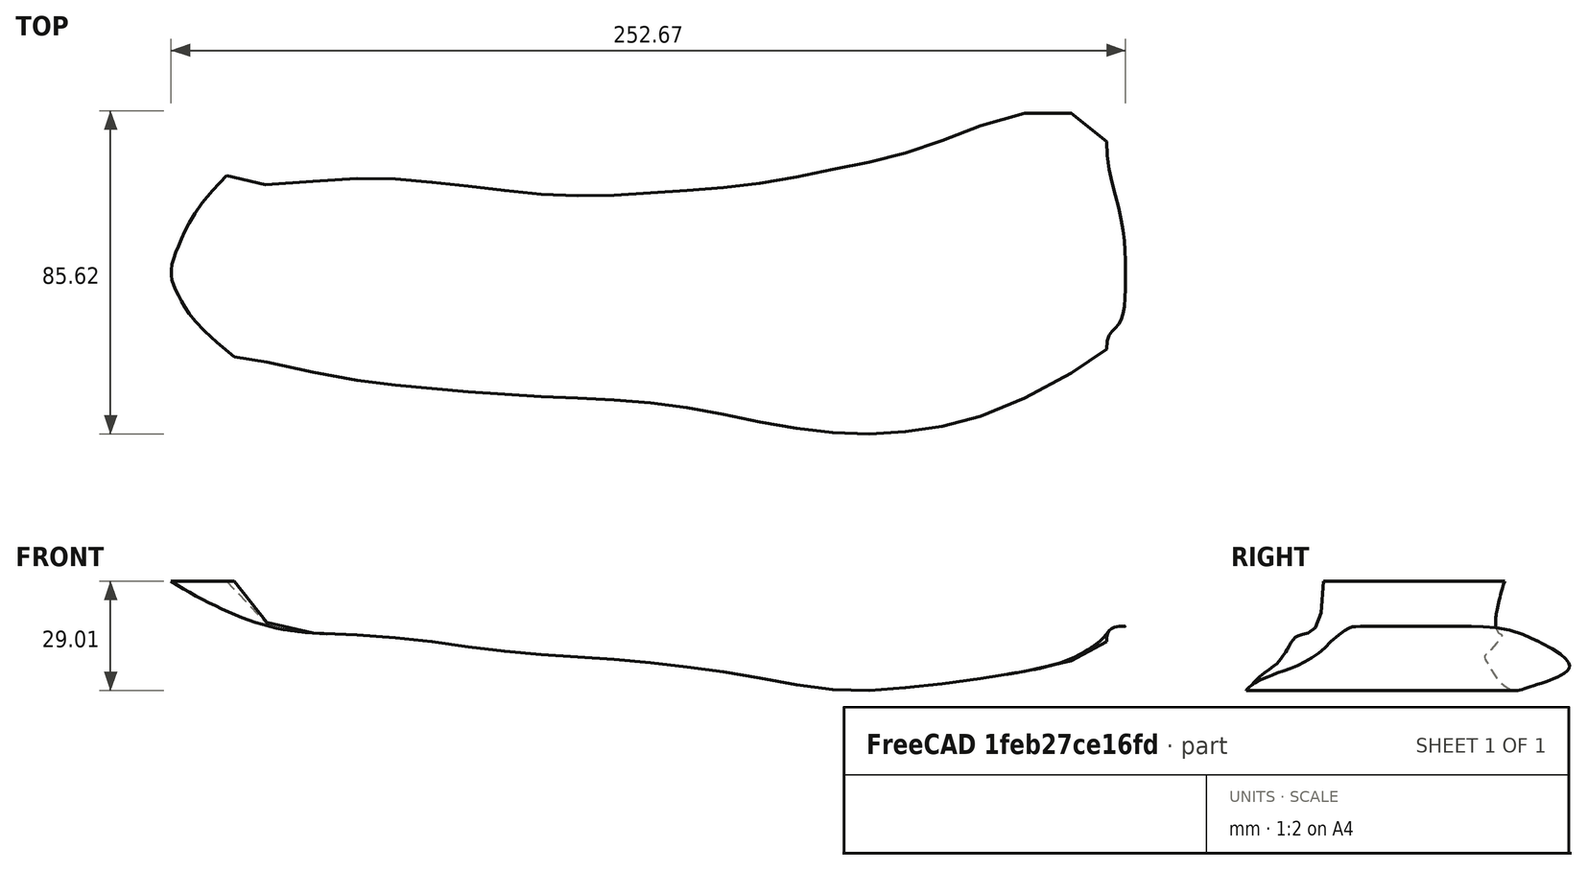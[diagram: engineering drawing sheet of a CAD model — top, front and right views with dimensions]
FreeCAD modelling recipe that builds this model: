
FCSTD DOCUMENT  (FreeCAD 0.17R10993 (Git))
Label: breitev3
License: All rights reserved
LicenseURL: http://en.wikipedia.org/wiki/All_rights_reserved
objects: Part::Spline×1, Sketcher::SketchObject×1
note: 2 computed .brp shape members not serialized (recipe doc carries the construction recipe); baked Part::Feature solids carry a one-line shape summary decoded from their .brp

FEATURE [Part::Spline] orig
FEATURE [Sketcher::SketchObject] Sketch
  sketch-geometry (39):
    g0: LineSegment StartX=0 StartY=0 StartZ=0 EndX=8.26111 EndY=-22.6773 EndZ=0
    g1: LineSegment StartX=8.26111 StartY=-22.6773 StartZ=0 EndX=22.7 EndY=-33.51 EndZ=0
    g2: LineSegment StartX=22.7 StartY=-33.51 StartZ=0 EndX=35.4471 EndY=-35.9623 EndZ=0
    g3: LineSegment StartX=35.4471 StartY=-35.9623 StartZ=0 EndX=75.0666 EndY=-38.4166 EndZ=0
    g4: LineSegment StartX=75.0666 StartY=-38.4166 StartZ=0 EndX=86.5145 EndY=-42.2733 EndZ=0
    g5: LineSegment StartX=86.5145 StartY=-42.2733 StartZ=0 EndX=104.128 EndY=-67.4573 EndZ=0
    g6: LineSegment StartX=104.128 StartY=-67.4573 StartZ=0 EndX=130.341 EndY=-42.2733 EndZ=0
    g7: LineSegment StartX=130.341 StartY=-42.2733 StartZ=0 EndX=152.808 EndY=-47.8831 EndZ=0
    g8: LineSegment StartX=152.808 StartY=-47.8831 StartZ=0 EndX=176.868 EndY=-52.0905 EndZ=0
    g9: LineSegment StartX=176.868 StartY=-52.0905 StartZ=0 EndX=196.607 EndY=-48.935 EndZ=0
    g10: LineSegment StartX=196.607 StartY=-48.935 StartZ=0 EndX=223.254 EndY=-44.377 EndZ=0
    g11: LineSegment StartX=223.254 StartY=-44.377 StartZ=0 EndX=241.335 EndY=-30.703 EndZ=0
    g12: LineSegment StartX=241.335 StartY=-30.703 StartZ=0 EndX=257.942 EndY=-22.7532 EndZ=0
    g13: LineSegment StartX=257.942 StartY=-22.7532 StartZ=0 EndX=261.471 EndY=0 EndZ=0
    g14: LineSegment StartX=261.471 StartY=0 StartZ=0 EndX=256.563 EndY=32.4076 EndZ=0
    g15: LineSegment StartX=256.563 StartY=32.4076 StartZ=0 EndX=241.335 EndY=35.7142 EndZ=0
    g16: LineSegment StartX=241.335 StartY=35.7142 StartZ=0 EndX=223.254 EndY=50.6395 EndZ=0
    g17: LineSegment StartX=223.254 StartY=50.6395 StartZ=0 EndX=196.607 EndY=49.2371 EndZ=0
    g18: LineSegment StartX=196.607 StartY=49.2371 StartZ=0 EndX=176.868 EndY=77.6735 EndZ=0
    g19: LineSegment StartX=176.868 StartY=77.6735 StartZ=0 EndX=152.808 EndY=60.9358 EndZ=0
    g20: LineSegment StartX=152.808 StartY=60.9358 StartZ=0 EndX=130.341 EndY=48.54 EndZ=0
    g21: LineSegment StartX=130.341 StartY=48.54 StartZ=0 EndX=104.128 EndY=48.54 EndZ=0
    g22: LineSegment StartX=104.128 StartY=48.54 StartZ=0 EndX=86.5145 EndY=48.54 EndZ=0
    g23: LineSegment StartX=86.5145 StartY=48.54 StartZ=0 EndX=75.0666 EndY=65.98 EndZ=0
    g24: LineSegment StartX=75.0666 StartY=65.98 StartZ=0 EndX=35.4471 EndY=52.6551 EndZ=0
    g25: LineSegment StartX=35.4471 StartY=52.6551 StartZ=0 EndX=22.7 EndY=46.78 EndZ=0
    g26: LineSegment StartX=22.7 StartY=46.78 StartZ=0 EndX=8.32753 EndY=38.37 EndZ=0
    g27: LineSegment StartX=8.32753 StartY=38.37 StartZ=0 EndX=0 EndY=0 EndZ=0
    g28: LineSegment StartX=22.7 StartY=46.78 StartZ=0 EndX=22.7 EndY=-33.51 EndZ=0
    g29: LineSegment StartX=35.4471 StartY=52.6551 StartZ=0 EndX=35.4471 EndY=-35.9623 EndZ=0
    g30: LineSegment StartX=75.0666 StartY=65.98 StartZ=0 EndX=75.0666 EndY=-38.4166 EndZ=0
    g31: LineSegment StartX=86.5145 StartY=48.54 StartZ=0 EndX=86.5145 EndY=-42.2733 EndZ=0
    g32: LineSegment StartX=104.128 StartY=48.54 StartZ=0 EndX=104.128 EndY=-67.4573 EndZ=0
    g33: LineSegment StartX=130.341 StartY=48.54 StartZ=0 EndX=130.341 EndY=-42.2733 EndZ=0
    g34: LineSegment StartX=152.808 StartY=60.9358 StartZ=0 EndX=152.808 EndY=-47.8831 EndZ=0
    g35: LineSegment StartX=176.868 StartY=77.6735 StartZ=0 EndX=176.868 EndY=-52.0905 EndZ=0
    g36: LineSegment StartX=196.607 StartY=49.2371 StartZ=0 EndX=196.607 EndY=-48.935 EndZ=0
    g37: LineSegment StartX=223.254 StartY=50.6395 StartZ=0 EndX=223.254 EndY=-44.377 EndZ=0
    g38: LineSegment StartX=241.335 StartY=35.7142 StartZ=0 EndX=241.335 EndY=-30.703 EndZ=0
  constraints (86):
    c: Coincident(g-1,g0)
    c: Coincident(g0,g1)
    c: Coincident(g1,g2)
    c: Coincident(g2,g3)
    c: Coincident(g3,g4)
    c: Coincident(g4,g5)
    c: Coincident(g5,g6)
    c: Coincident(g6,g7)
    c: Coincident(g7,g8)
    c: Coincident(g8,g9)
    c: Coincident(g9,g10)
    c: Coincident(g10,g11)
    c: Coincident(g11,g12)
    c: Coincident(g12,g13)
    c: PointOnObject(g13,g-1)
    c: Coincident(g13,g14)
    c: Coincident(g14,g15)
    c: Coincident(g15,g16)
    c: Coincident(g16,g17)
    c: Coincident(g17,g18)
    c: Coincident(g18,g19)
    c: Coincident(g19,g20)
    c: Coincident(g20,g21)
    c: Coincident(g21,g22)
    c: Coincident(g22,g23)
    c: Coincident(g23,g24)
    c: Coincident(g24,g25)
    c: Coincident(g25,g26)
    c: Coincident(g26,g27)
    c: Coincident(g27,g0)
    c: Coincident(g28,g25)
    c: Coincident(g28,g1)
    c: Vertical(g28)
    c: Coincident(g29,g24)
    c: Coincident(g29,g2)
    c: Vertical(g29)
    c: Coincident(g30,g23)
    c: Coincident(g30,g3)
    c: Coincident(g31,g22)
    c: Coincident(g31,g4)
    c: Vertical(g31)
    c: Coincident(g32,g21)
    c: Coincident(g32,g5)
    c: Vertical(g32)
    c: Coincident(g33,g20)
    c: Coincident(g33,g6)
    c: Vertical(g33)
    c: Coincident(g34,g19)
    c: Coincident(g34,g7)
    c: Vertical(g34)
    c: Coincident(g35,g18)
    c: Coincident(g35,g8)
    c: Vertical(g35)
    c: Coincident(g36,g9)
    c: Vertical(g36)
    c: Coincident(g37,g16)
    c: Coincident(g37,g10)
    c: Vertical(g37)
    c: Coincident(g38,g15)
    c: Coincident(g38,g11)
    c: Vertical(g38)
    c: Vertical(g30)
    c: DistanceY(g26) = 38.37  'l1'
    c: DistanceY(g25) = 46.78  'l2'
    c: DistanceY(g24) = 52.6551  'l3'
    c: DistanceY(g23) = 65.98  'l4'
    c: DistanceY(g22) = 48.54  'l5'
    c: DistanceY(g21) = 48.54  'l6'
    c: DistanceY(g20) = 48.54  'l7'
    c: DistanceY(g19) = 60.9358  'l8'
    c: DistanceY(g18) = 77.6735  'l9'
    c: DistanceY(g17) = 49.2371  'l10'
    c: DistanceY(g16) = 50.6395  'l11'
    c: DistanceY(g15) = 35.7142  'l12'
    c: DistanceY(g0) = -22.6773  'r1'
    c: DistanceY(g1) = -33.51  'r2'
    c: DistanceY(g2) = -35.9623  'r3'
    c: DistanceY(g3) = -38.4166  'r4'
    c: DistanceY(g4) = -42.2733  'r5'
    c: DistanceY(g5) = -67.4573  'r6'
    c: DistanceY(g6) = -42.2733  'r7'
    c: DistanceY(g7) = -47.8831  'r8'
    c: DistanceY(g8) = -52.0905  'r9'
    c: DistanceY(g9) = -48.935  'r10'
    c: DistanceY(g10) = -44.377  'r11'
    c: DistanceY(g11) = -30.703  'r12'
